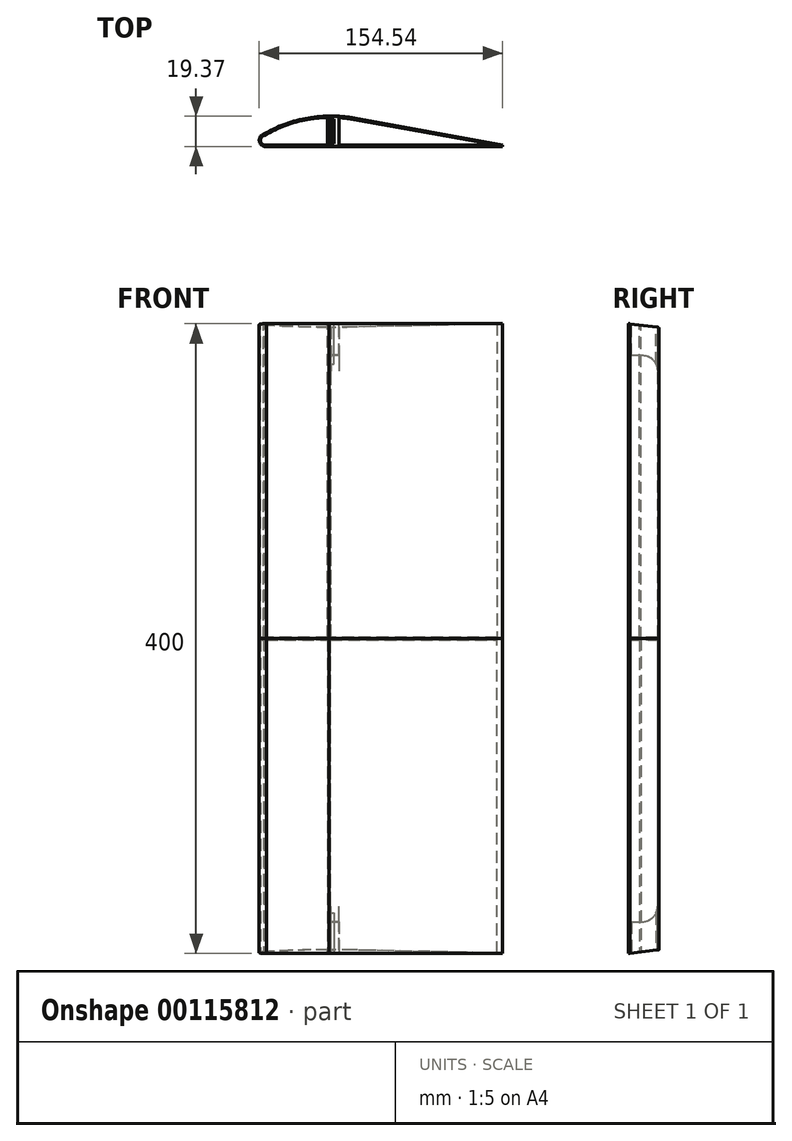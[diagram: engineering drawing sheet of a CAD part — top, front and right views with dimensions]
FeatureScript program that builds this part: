
annotation { "Feature Type Name" : "Feature", "Feature Type Description" : "" }
export const myFeature = defineFeature(function(context is Context, id is Id, definition is map)
    precondition{}
    {
        {
            var Q0;
            Q0=qCreatedBy(makeId("Top.planeOp"),FACE);
            var sketch = newSketch(context, id + "F0", { "sketchPlane" : qUnion([Q0])});
            skLineSegment(sketch, "E0", {"start": v(94.17, -2) * mm, "end": v(0, 15) * mm});
            skLineSegment(sketch, "E1", {"start": v(-55.86, -3) * mm, "end": v(94.14, -3) * mm});
            skLineSegment(sketch, "E2", {"start": v(94.14, -3) * mm, "end": v(94.17, -2) * mm});
            skArc(sketch, "E3", {"start": v(0, 15) * mm, "mid": v(-29.67, 15.05) * mm, "end": v(-57.5, 4.8) * mm});
            skArc(sketch, "E4", {"start": v(-57.5, 4.8) * mm, "mid": v(-60.28, 0.14) * mm, "end": v(-55.86, -3) * mm});
            skLineSegment(sketch, "E5", {"start": v(-16.04, 16.33) * mm, "end": v(-16.04, -3) * mm});
            skSolve(sketch);
        }
        {
            var Q0;
            {var subQ1=sQuery(id+"F0.wireOp",EDGE,"E0");Q0=makeQuery(id+"F0.imprint","IMPRINT",FACE,{"disambiguationData":[TD([[makeQuery(id+"F0.imprint","IMPRINT",EDGE,{"derivedFrom":subQ1}),1.0]])]});}
            extrude(context, id + "F1", {"entities" : qUnion([Q0]), "depth" : 200 * mm});
        }
        {
            var Q0;
            Q0=makeQuery(id+"F1.opExtrude","CAP_FACE",FACE,{"disambiguationData":[OSD([sQuery(id+"F0.wireOp",EDGE,"E0"),sQuery(id+"F0.wireOp",EDGE,"E1"),sQuery(id+"F0.wireOp",EDGE,"E2"),sQuery(id+"F0.wireOp",EDGE,"E3"),sQuery(id+"F0.wireOp",EDGE,"E4")])],"isStart":false});
            var sketch = newSketch(context, id + "F2", { "sketchPlane" : qUnion([Q0])});
            skLineSegment(sketch, "E6", {"start": v(94.17, -2) * mm, "end": v(0, 15) * mm});
            skLineSegment(sketch, "E7", {"start": v(-55.86, -3) * mm, "end": v(94.14, -3) * mm});
            skLineSegment(sketch, "E8", {"start": v(94.14, -3) * mm, "end": v(94.17, -2) * mm});
            skArc(sketch, "E9", {"start": v(0, 15) * mm, "mid": v(-29.67, 15.05) * mm, "end": v(-57.5, 4.8) * mm});
            skArc(sketch, "E10", {"start": v(-57.5, 4.8) * mm, "mid": v(-60.28, 0.14) * mm, "end": v(-55.86, -3) * mm});
            skLineSegment(sketch, "E11", {"start": v(-16.04, 16.33) * mm, "end": v(-16.04, -3) * mm});
            skSolve(sketch);
        }
        {
            var Q0;
            {var subQ2=sQuery(id+"F2.wireOp",EDGE,"E10");Q0=makeQuery(id+"F2.imprint","IMPRINT",FACE,{"disambiguationData":[TD([[makeQuery(id+"F2.imprint","IMPRINT",EDGE,{"derivedFrom":subQ2}),1.0]])]});}
            extrude(context, id + "F3", {"entities" : qUnion([Q0]), "oppositeDirection" : true, "depth" : 200 * mm});
        }
        {
            var Q0;
            Q0=makeQuery(id+"F1.opExtrude","CAP_FACE",FACE,{"disambiguationData":[OSD([sQuery(id+"F0.wireOp",EDGE,"E0"),sQuery(id+"F0.wireOp",EDGE,"E1"),sQuery(id+"F0.wireOp",EDGE,"E2"),sQuery(id+"F0.wireOp",EDGE,"E3"),sQuery(id+"F0.wireOp",EDGE,"E5")])],"isStart":false});
            var Q1;
            Q1=makeQuery(id+"F3.opExtrude","CAP_FACE",FACE,{"disambiguationData":[OSD([sQuery(id+"F2.wireOp",EDGE,"E7"),sQuery(id+"F2.wireOp",EDGE,"E9"),sQuery(id+"F2.wireOp",EDGE,"E10"),sQuery(id+"F2.wireOp",EDGE,"E11")])],"isStart":true});
            shell(context, id + "F4", {"entities" : qUnion([Q0, Q1]), "thickness" : .8 * mm});
        }
        {
            var Q0;
            Q0=makeQuery(id+"F1.opExtrude","CAP_FACE",FACE,{"disambiguationData":[OSD([sQuery(id+"F0.wireOp",EDGE,"E0"),sQuery(id+"F0.wireOp",EDGE,"E1"),sQuery(id+"F0.wireOp",EDGE,"E2"),sQuery(id+"F0.wireOp",EDGE,"E3"),sQuery(id+"F0.wireOp",EDGE,"E5")])],"isStart":false});
            var sketch = newSketch(context, id + "F5", { "sketchPlane" : qUnion([Q0])});
            skLineSegment(sketch, "E12.bottom", {"start": v(-12.74, -2.2) * mm, "end": v(-9.74, -2.2) * mm});
            skLineSegment(sketch, "E12.top", {"start": v(-12.74, 15.54) * mm, "end": v(-9.74, 15.54) * mm});
            skLineSegment(sketch, "E12.left", {"start": v(-12.74, -2.2) * mm, "end": v(-12.74, 15.54) * mm});
            skLineSegment(sketch, "E12.right", {"start": v(-9.74, -2.2) * mm, "end": v(-9.74, 15.54) * mm});
            skLineSegment(sketch, "E13.bottom", {"start": v(-12.74, 15.54) * mm, "end": v(-15.24, 15.54) * mm});
            skLineSegment(sketch, "E13.top", {"start": v(-12.74, 14.54) * mm, "end": v(-15.24, 14.54) * mm});
            skLineSegment(sketch, "E13.left", {"start": v(-12.74, 15.54) * mm, "end": v(-12.74, 14.54) * mm});
            skLineSegment(sketch, "E13.right", {"start": v(-15.24, 15.54) * mm, "end": v(-15.24, 14.54) * mm});
            skLineSegment(sketch, "E14.bottom", {"start": v(-12.74, -2.2) * mm, "end": v(-15.24, -2.2) * mm});
            skLineSegment(sketch, "E14.top", {"start": v(-12.74, -1.2) * mm, "end": v(-15.24, -1.2) * mm});
            skLineSegment(sketch, "E14.left", {"start": v(-12.74, -2.2) * mm, "end": v(-12.74, -1.2) * mm});
            skLineSegment(sketch, "E14.right", {"start": v(-15.24, -2.2) * mm, "end": v(-15.24, -1.2) * mm});
            skSolve(sketch);
        }
        {
            var Q0;
            Q0=qSketchRegion(id+"F5",true);
            extrude(context, id + "F6", {"entities" : qUnion([Q0]), "operationType" : NewBodyOperationType.ADD, "oppositeDirection" : true, "depth" : 20 * mm});
        }
        {
            var Q0;
            {var subQ0=sQuery(id+"F0.wireOp",EDGE,"E3");Q0=makeQuery(id+"F6.boolean.opBoolean","INTERSECT",EDGE,{"derivedFrom":[makeQuery(id+"FlvnLV0fvoY6EBe_2.boolean.opBoolean","MERGE",FACE,{"derivedFrom":[makeQuery(id+"F4.opShell","OFFSET_FACE",FACE,{"disambiguationData":[OSD([subQ0])]}),makeQuery(id+"FlvnLV0fvoY6EBe_2.opExtrude","SWEPT_FACE",FACE,{"disambiguationData":[OSD([subQ0])]})]}),makeQuery(id+"F6.opExtrude","CAP_FACE",FACE,{"disambiguationData":[OSD([sQuery(id+"F5.wireOp",EDGE,"E12.bottom"),sQuery(id+"F5.wireOp",EDGE,"E12.top"),sQuery(id+"F5.wireOp",EDGE,"E12.left"),sQuery(id+"F5.wireOp",EDGE,"E12.right")])],"isStart":false})]});}
            var Q1;
            Q1=makeQuery(id+"F6.opExtrude","CAP_EDGE",EDGE,{"disambiguationData":[OSD([sQuery(id+"F5.wireOp",EDGE,"E12.bottom")])],"isStart":false});
            fillet(context, id + "F7", {"entities" : qUnion([Q0, Q1]), "radius" : 10 * mm, "tangentPropagation" : true, "allowEdgeOverflow" : false});
        }
        {
            var Q0;
            Q0=makeQuery(id+"F6.boolean.opBoolean","MERGE",FACE,{"derivedFrom":[makeQuery(id+"F1.opExtrude","CAP_FACE",FACE,{"disambiguationData":[OSD([sQuery(id+"F0.wireOp",EDGE,"E0"),sQuery(id+"F0.wireOp",EDGE,"E1"),sQuery(id+"F0.wireOp",EDGE,"E2"),sQuery(id+"F0.wireOp",EDGE,"E3"),sQuery(id+"F0.wireOp",EDGE,"E5")])],"isStart":false}),makeQuery(id+"F6.opExtrude","CAP_FACE",FACE,{"disambiguationData":[OSD([sQuery(id+"F5.wireOp",EDGE,"E12.bottom"),sQuery(id+"F5.wireOp",EDGE,"E12.top"),sQuery(id+"F5.wireOp",EDGE,"E12.left"),sQuery(id+"F5.wireOp",EDGE,"E12.right"),sQuery(id+"F5.wireOp",EDGE,"E13.bottom"),sQuery(id+"F5.wireOp",EDGE,"E13.top"),sQuery(id+"F5.wireOp",EDGE,"E13.right"),sQuery(id+"F5.wireOp",EDGE,"E14.bottom"),sQuery(id+"F5.wireOp",EDGE,"E14.top"),sQuery(id+"F5.wireOp",EDGE,"E14.right")])],"isStart":true})]});
            var sketch = newSketch(context, id + "F8", { "sketchPlane" : qUnion([Q0])});
            skLineSegment(sketch, "E15.bottom", {"start": v(94.14, -3) * mm, "end": v(-61.05, -3) * mm});
            skLineSegment(sketch, "E15.top", {"start": v(94.14, 19.34) * mm, "end": v(-61.05, 19.34) * mm});
            skLineSegment(sketch, "E15.left", {"start": v(94.14, -3) * mm, "end": v(94.14, 19.34) * mm});
            skLineSegment(sketch, "E15.right", {"start": v(-61.05, -3) * mm, "end": v(-61.05, 19.34) * mm});
            skSolve(sketch);
        }
        {
            var Q0;
            Q0=qSketchRegion(id+"F8",true);
            var Q1;
            Q1=sQuery(id+"F8.wireOp",EDGE,"E15.bottom");
            revolve(context, id + "F9", {"operationType" : NewBodyOperationType.REMOVE, "entities" : qUnion([Q0]), "axis" : qUnion([Q1]), "revolveType" : RevolveType.ONE_DIRECTION, "angle" : 7 * degree});
        }
        {
            var Q0;
            Q0=makeQuery(id+"F1.opExtrude","SWEPT_BODY",BODY,{"disambiguationData":[OSD([sQuery(id+"F0.wireOp",EDGE,"E0"),sQuery(id+"F0.wireOp",EDGE,"E1"),sQuery(id+"F0.wireOp",EDGE,"E2"),sQuery(id+"F0.wireOp",EDGE,"E3"),sQuery(id+"F0.wireOp",EDGE,"E5")])]});
            var Q1;
            Q1=makeQuery(id+"F3.opExtrude","SWEPT_BODY",BODY,{"disambiguationData":[OSD([sQuery(id+"F2.wireOp",EDGE,"E7"),sQuery(id+"F2.wireOp",EDGE,"E9"),sQuery(id+"F2.wireOp",EDGE,"E10"),sQuery(id+"F2.wireOp",EDGE,"E11")])]});
            var Q2;
            Q2=qCreatedBy(makeId("Top.planeOp"),FACE);
            mirror(context, id + "F10", {"entities" : qUnion([Q0, Q1]), "mirrorPlane" : qUnion([Q2])});
        }
    });
